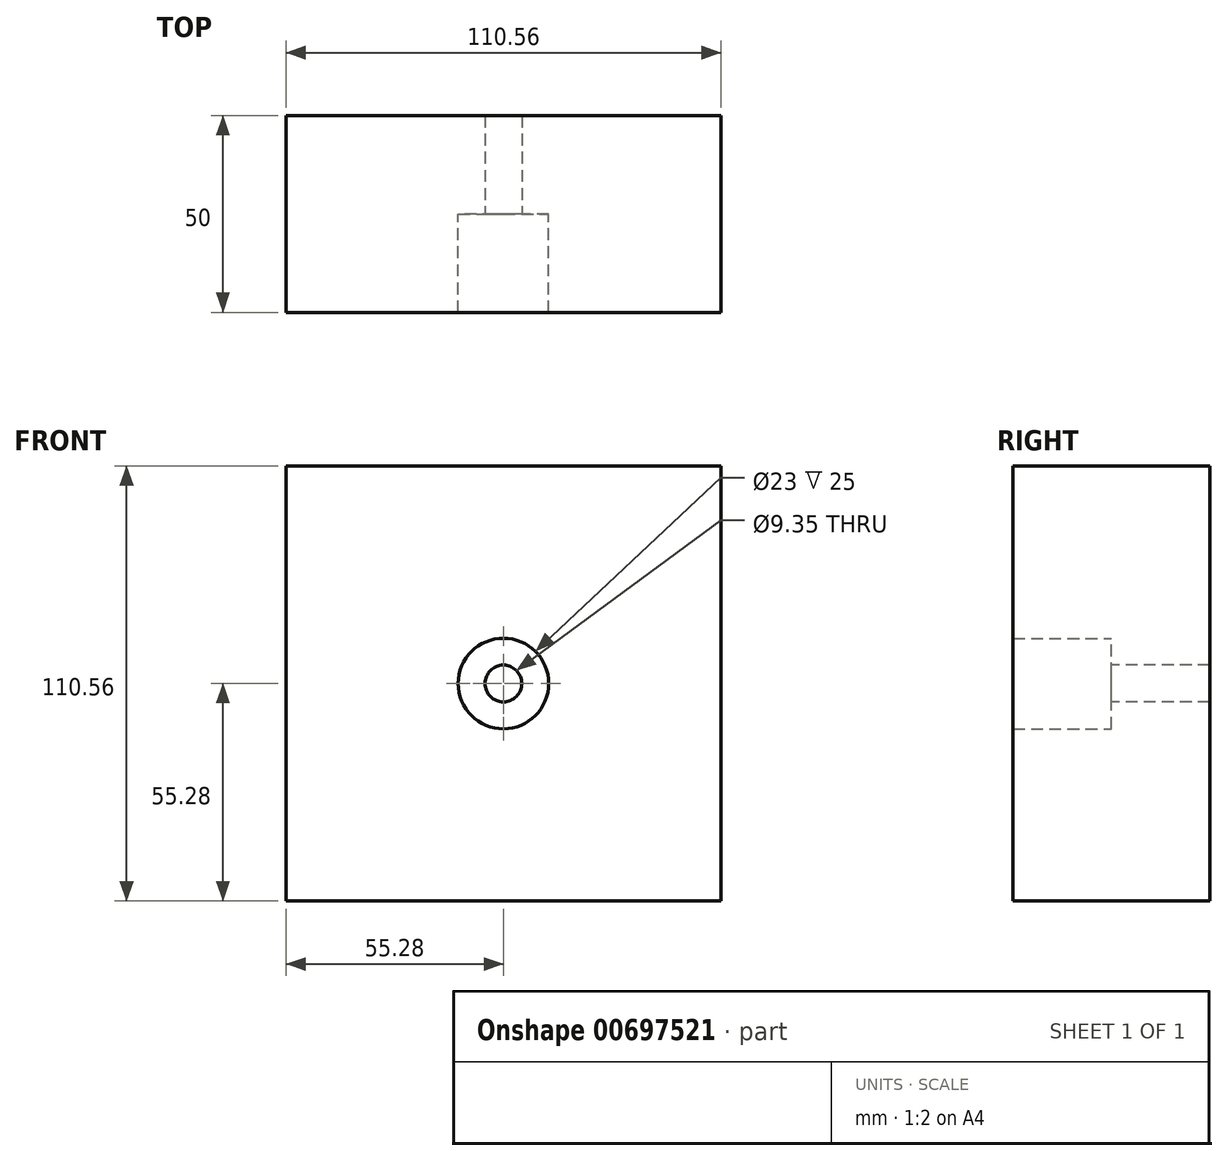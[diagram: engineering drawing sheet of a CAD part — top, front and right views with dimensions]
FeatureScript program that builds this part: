
annotation { "Feature Type Name" : "Feature", "Feature Type Description" : "" }
export const myFeature = defineFeature(function(context is Context, id is Id, definition is map)
    precondition{}
    {
        {
            var Q0;
            Q0=qCreatedBy(makeId("Front.planeOp"),FACE);
            var sketch = newSketch(context, id + "F0", { "sketchPlane" : qUnion([Q0])});
            skLineSegment(sketch, "E0.bottom", {"start": v(-55.28, 55.28) * mm, "end": v(55.28, 55.28) * mm});
            skLineSegment(sketch, "E0.top", {"start": v(-55.28, -55.28) * mm, "end": v(55.28, -55.28) * mm});
            skLineSegment(sketch, "E0.left", {"start": v(-55.28, 55.28) * mm, "end": v(-55.28, -55.28) * mm});
            skLineSegment(sketch, "E0.right", {"start": v(55.28, 55.28) * mm, "end": v(55.28, -55.28) * mm});
            skSolve(sketch);
        }
        {
            var Q0;
            Q0=makeQuery(id+"F0.imprint","IMPRINT",FACE,{"disambiguationData":[TD([[makeQuery(id+"F0.imprint","IMPRINT",EDGE,{"derivedFrom":sQuery(id+"F0.wireOp",EDGE,"E0.bottom")}),-1.0]])]});
            extrude(context, id + "F1", {"entities" : qUnion([Q0]), "endBound" : BoundingType.SYMMETRIC, "depth" : 50 * mm, "offsetDistance" : 25 * mm});
        }
        {
            var Q0;
            Q0=qCreatedBy(makeId("Front.planeOp"),FACE);
            var sketch = newSketch(context, id + "F2", { "sketchPlane" : qUnion([Q0])});
            skCircle(sketch, "E1", {"center": v(0, 0) * mm, "radius": 11.5 * mm});
            skSolve(sketch);
        }
        {
            var Q0;
            Q0 = qSketchRegion(id + "F2", true);
            extrude(context, id + "F3", {"entities" : qUnion([Q0]), "operationType" : NewBodyOperationType.REMOVE, "endBound" : BoundingType.UP_TO_NEXT, "depth" : 25 * mm, "offsetDistance" : 25 * mm});
        }
        {
            var Q0;
            Q0=makeQuery(id+"F3.boolean.opBoolean","COPY",FACE,{"derivedFrom":makeQuery(id+"F3.opExtrude","CAP_FACE",FACE,{"disambiguationData":[OSD([sQuery(id+"F2.wireOp",EDGE,"E1")])],"isStart":true})});
            var sketch = newSketch(context, id + "F4", { "sketchPlane" : qUnion([Q0])});
            skCircle(sketch, "E2", {"center": v(0, 0) * mm, "radius": 4.67 * mm});
            skSolve(sketch);
        }
        {
            var Q0;
            Q0=makeQuery(id+"F4.imprint","IMPRINT",FACE,{"disambiguationData":[TD([[makeQuery(id+"F4.imprint","IMPRINT",EDGE,{"derivedFrom":sQuery(id+"F4.wireOp",EDGE,"E2")}),1.0]])]});
            extrude(context, id + "F5", {"entities" : qUnion([Q0]), "operationType" : NewBodyOperationType.REMOVE, "endBound" : BoundingType.UP_TO_NEXT, "oppositeDirection" : true, "depth" : 25 * mm, "offsetDistance" : 25 * mm});
        }
    });
